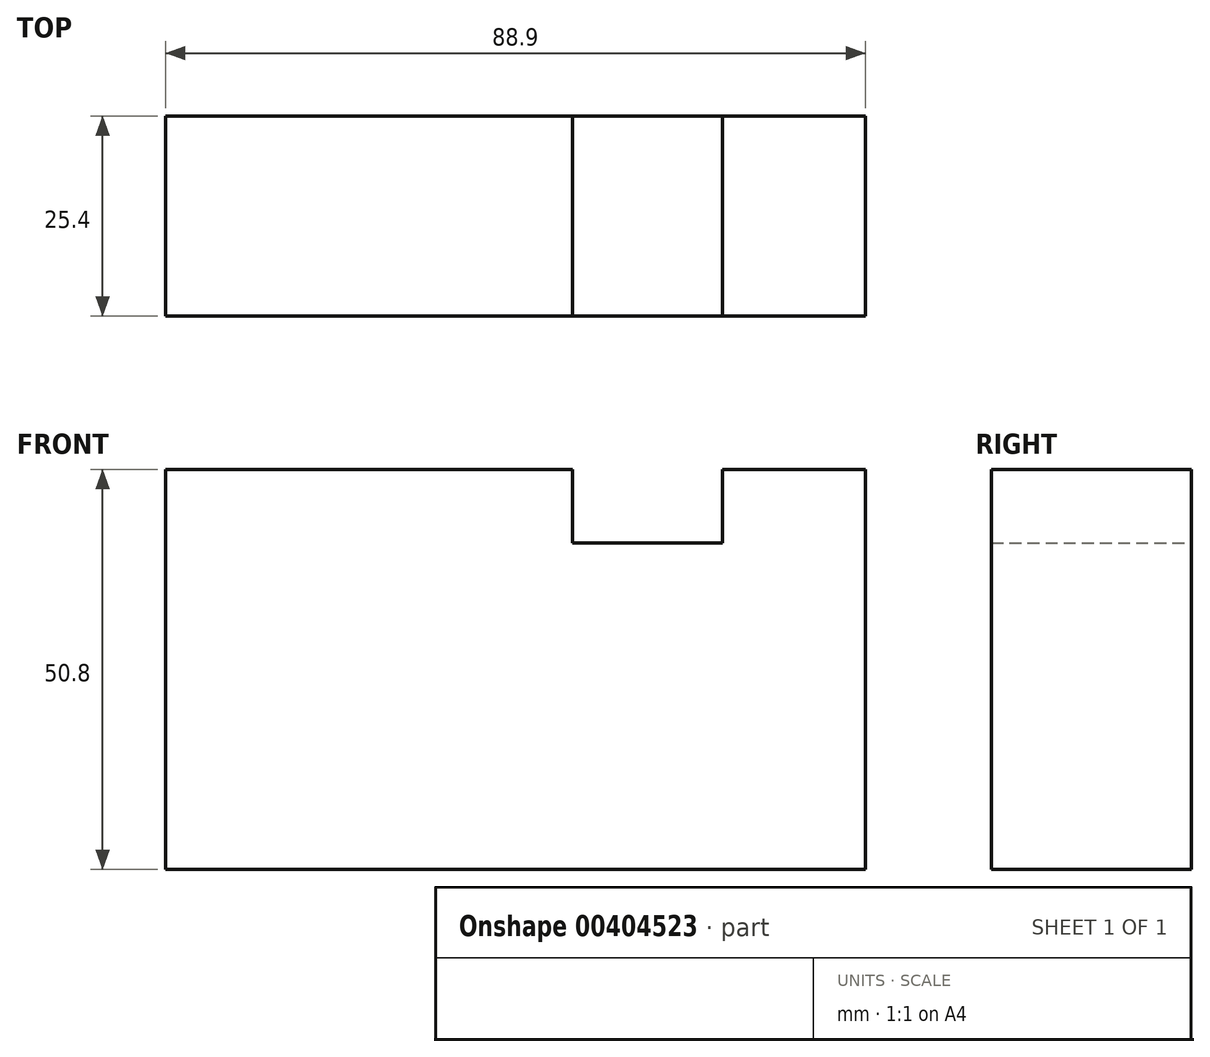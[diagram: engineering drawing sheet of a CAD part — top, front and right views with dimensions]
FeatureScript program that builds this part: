
annotation { "Feature Type Name" : "Feature", "Feature Type Description" : "" }
export const myFeature = defineFeature(function(context is Context, id is Id, definition is map)
    precondition{}
    {
        {
            var Q0;
            Q0=qCreatedBy(makeId("Front.planeOp"),FACE);
            var sketch = newSketch(context, id + "F0", { "sketchPlane" : qUnion([Q0])});
            skLineSegment(sketch, "E0.bottom", {"start": v(-44.45, -25.4) * mm, "end": v(44.45, -25.4) * mm});
            skLineSegment(sketch, "E0.top", {"start": v(-44.45, 25.4) * mm, "end": v(44.45, 25.4) * mm});
            skLineSegment(sketch, "E0.left", {"start": v(-44.45, -25.4) * mm, "end": v(-44.45, 25.4) * mm});
            skLineSegment(sketch, "E0.right", {"start": v(44.45, -25.4) * mm, "end": v(44.45, 25.4) * mm});
            skPoint(sketch, "E0.middle", {"position": v(0, 0) * mm});
            skLineSegment(sketch, "E1.bottom", {"start": v(41.17, 47.2) * mm, "end": v(89.5, 47.2) * mm});
            skLineSegment(sketch, "E1.top", {"start": v(41.17, 91.01) * mm, "end": v(89.5, 91.01) * mm});
            skLineSegment(sketch, "E1.left", {"start": v(41.17, 47.2) * mm, "end": v(41.17, 91.01) * mm});
            skLineSegment(sketch, "E1.right", {"start": v(89.5, 47.2) * mm, "end": v(89.5, 91.01) * mm});
            skPoint(sketch, "E1.middle", {"position": v(65.34, 69.1) * mm});
            skLineSegment(sketch, "E2", {"start": v(26.3, 47.9) * mm, "end": v(26.3, 16.1) * mm});
            skArc(sketch, "E3", {"start": v(26.3, 47.9) * mm, "mid": v(30.32, 56.43) * mm, "end": v(39.46, 58.75) * mm});
            skLineSegment(sketch, "E4", {"start": v(39.46, 58.75) * mm, "end": v(62.8, 58.75) * mm});
            skLineSegment(sketch, "E5.0", {"start": v(40.84, 77.8) * mm, "end": v(62.8, 77.8) * mm});
            skArc(sketch, "E5.1", {"start": v(7.25, 47.9) * mm, "mid": v(17.34, 70.38) * mm, "end": v(40.84, 77.8) * mm});
            skLineSegment(sketch, "E5.2", {"start": v(7.25, 47.9) * mm, "end": v(7.25, 16.1) * mm});
            skLineSegment(sketch, "E6", {"start": v(62.8, 58.75) * mm, "end": v(62.8, 77.8) * mm});
            skLineSegment(sketch, "E7", {"start": v(7.25, 16.1) * mm, "end": v(26.3, 16.1) * mm});
            skSolve(sketch);
        }
        {
            var Q0;
            Q0=makeQuery(id+"F0.imprint","IMPRINT",FACE,{"disambiguationData":[TD([[makeQuery(id+"F0.imprint","IMPRINT",EDGE,{"derivedFrom":sQuery(id+"F0.wireOp",EDGE,"E0.bottom")}),1.0]])]});
            extrude(context, id + "F1", {"entities" : qUnion([Q0]), "endBound" : BoundingType.SYMMETRIC, "depth" : 25.4 * mm});
        }
    });
